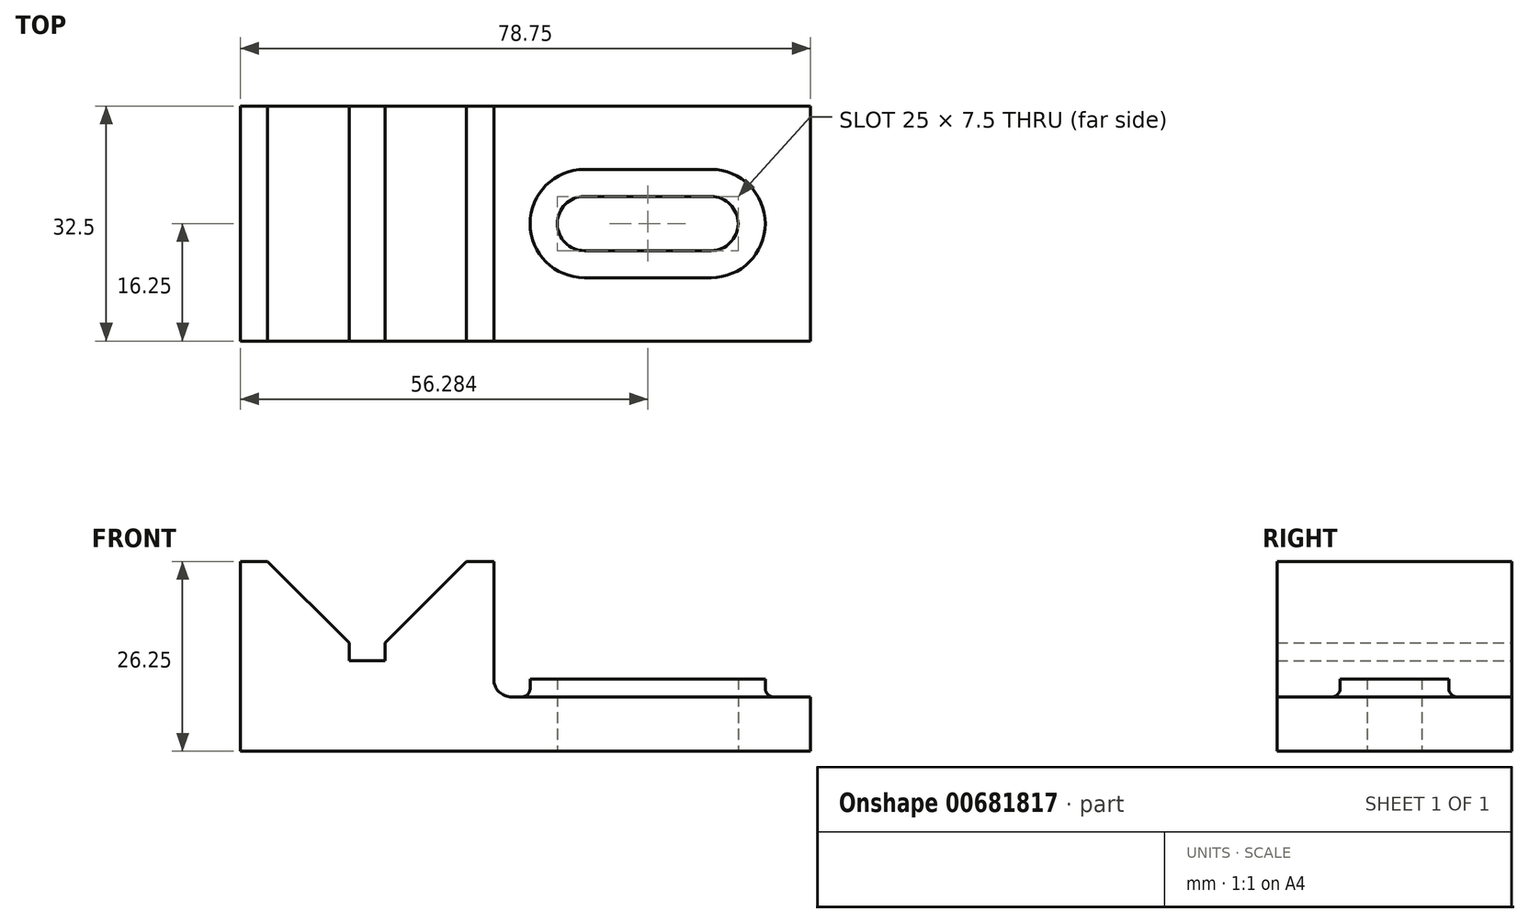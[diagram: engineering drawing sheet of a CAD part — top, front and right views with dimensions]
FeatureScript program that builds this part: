
annotation { "Feature Type Name" : "Feature", "Feature Type Description" : "" }
export const myFeature = defineFeature(function(context is Context, id is Id, definition is map)
    precondition{}
    {
        {
            var Q0;
            Q0=qCreatedBy(makeId("Front.planeOp"),FACE);
            var sketch = newSketch(context, id + "F0", { "sketchPlane" : qUnion([Q0])});
            skLineSegment(sketch, "E0", {"start": v(-60.82, 38.77) * mm, "end": v(-60.82, 12.52) * mm});
            skLineSegment(sketch, "E1", {"start": v(-60.82, 12.52) * mm, "end": v(17.93, 12.52) * mm});
            skLineSegment(sketch, "E2", {"start": v(17.93, 12.52) * mm, "end": v(17.93, 20.02) * mm});
            skLineSegment(sketch, "E3", {"start": v(17.93, 20.02) * mm, "end": v(-25.82, 20.02) * mm});
            skLineSegment(sketch, "E4", {"start": v(-25.82, 20.02) * mm, "end": v(-25.82, 38.77) * mm});
            skLineSegment(sketch, "E5", {"start": v(-25.82, 38.77) * mm, "end": v(-29.57, 38.77) * mm});
            skLineSegment(sketch, "E6", {"start": v(-29.57, 38.77) * mm, "end": v(-40.82, 27.52) * mm});
            skLineSegment(sketch, "E7", {"start": v(-45.82, 27.52) * mm, "end": v(-57.07, 38.77) * mm});
            skLineSegment(sketch, "E8", {"start": v(-57.07, 38.77) * mm, "end": v(-60.82, 38.77) * mm});
            skLineSegment(sketch, "E9", {"start": v(-45.82, 27.52) * mm, "end": v(-45.82, 25.02) * mm});
            skLineSegment(sketch, "E10", {"start": v(-45.82, 25.02) * mm, "end": v(-40.82, 25.02) * mm});
            skLineSegment(sketch, "E11", {"start": v(-40.82, 25.02) * mm, "end": v(-40.82, 27.52) * mm});
            skSolve(sketch);
        }
        {
            var Q0;
            Q0 = qSketchRegion(id + "F0", true);
            extrude(context, id + "F1", {"entities" : qUnion([Q0]), "depth" : 32.5 * mm, "offsetDistance" : 25 * mm});
        }
        {
            var Q0;
            Q0=makeQuery(id+"F1.opExtrude","SWEPT_FACE",FACE,{"disambiguationData":[OSD([sQuery(id+"F0.wireOp",EDGE,"E3")])]});
            var sketch = newSketch(context, id + "F2", { "sketchPlane" : qUnion([Q0])});
            skPoint(sketch, "E12", {"position": v(17.93, -16.25) * mm});
            skPoint(sketch, "E13", {"position": v(-3.95, -16.25) * mm});
            skArc(sketch, "E14", {"start": v(-13.29, -12.5) * mm, "mid": v(-17.04, -16.25) * mm, "end": v(-13.29, -20) * mm});
            skArc(sketch, "E15", {"start": v(-13.29, -8.75) * mm, "mid": v(-20.79, -16.25) * mm, "end": v(-13.29, -23.75) * mm});
            skArc(sketch, "E16", {"start": v(4.21, -20) * mm, "mid": v(7.96, -16.25) * mm, "end": v(4.21, -12.5) * mm});
            skArc(sketch, "E17", {"start": v(4.21, -23.75) * mm, "mid": v(11.71, -16.25) * mm, "end": v(4.21, -8.75) * mm});
            skLineSegment(sketch, "E18", {"start": v(-13.29, -8.75) * mm, "end": v(4.21, -8.75) * mm});
            skLineSegment(sketch, "E19", {"start": v(4.21, -23.75) * mm, "end": v(-13.29, -23.75) * mm});
            skLineSegment(sketch, "E20", {"start": v(-13.29, -12.5) * mm, "end": v(4.21, -12.5) * mm});
            skLineSegment(sketch, "E21", {"start": v(4.21, -20) * mm, "end": v(-13.29, -20) * mm});
            skSolve(sketch);
        }
        {
            var Q0;
            Q0 = qSketchRegion(id + "F2", true);
            extrude(context, id + "F3", {"entities" : qUnion([Q0]), "operationType" : NewBodyOperationType.ADD, "depth" : 2.5 * mm, "offsetDistance" : 25 * mm});
        }
        {
            var Q0;
            Q0=makeQuery(id+"F3.boolean.opBoolean","SPLIT",FACE,{"disambiguationData":[TD([makeQuery(id+"F3.opExtrude","SWEPT_FACE",FACE,{"disambiguationData":[OSD([sQuery(id+"F2.wireOp",EDGE,"E14")])]})])],"derivedFrom":makeQuery(id+"F1.opExtrude","SWEPT_FACE",FACE,{"disambiguationData":[OSD([sQuery(id+"F0.wireOp",EDGE,"E3")])]})});
            extrude(context, id + "F4", {"entities" : qUnion([Q0]), "operationType" : NewBodyOperationType.REMOVE, "oppositeDirection" : true, "depth" : 25 * mm, "offsetDistance" : 25 * mm});
        }
        {
            var Q0;
            Q0=makeQuery(id+"F1.opExtrude","SWEPT_EDGE",EDGE,{"disambiguationData":[OSD([sQuery(id+"F0.wireOp",EDGE,"E3"),sQuery(id+"F0.wireOp",EDGE,"E4")])]});
            fillet(context, id + "F5", {"entities" : qUnion([Q0]), "radius" : 2.5 * mm, "tangentPropagation" : true, "allowEdgeOverflow" : false});
        }
        {
            var Q0;
            Q0=makeQuery(id+"F3.opExtrude","CAP_EDGE",EDGE,{"disambiguationData":[OSD([sQuery(id+"F2.wireOp",EDGE,"E19")])],"isStart":true});
            fillet(context, id + "F6", {"entities" : qUnion([Q0]), "radius" : 1.25 * mm, "tangentPropagation" : true, "allowEdgeOverflow" : false});
        }
    });
